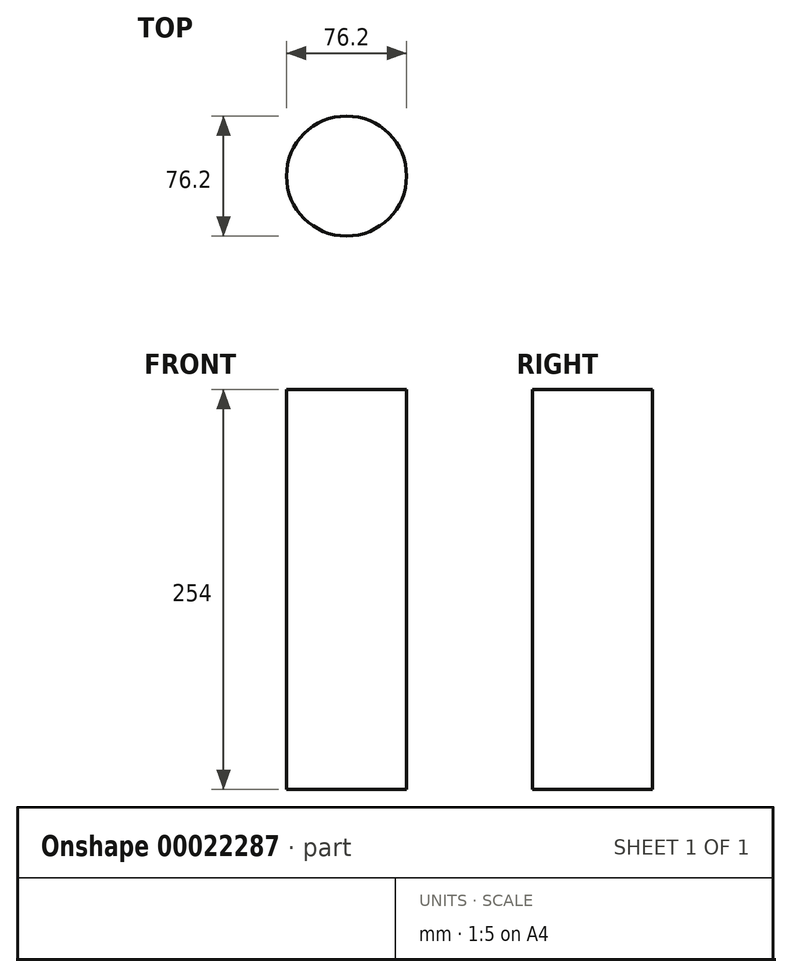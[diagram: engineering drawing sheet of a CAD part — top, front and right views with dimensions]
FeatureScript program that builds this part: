
annotation { "Feature Type Name" : "Feature", "Feature Type Description" : "" }
export const myFeature = defineFeature(function(context is Context, id is Id, definition is map)
    precondition{}
    {
        {
            var Q0;
            Q0=qCreatedBy(makeId("Top.planeOp"),FACE);
            var sketch = newSketch(context, id + "F0", { "sketchPlane" : qUnion([Q0])});
            skCircle(sketch, "E0", {"center": v(0, 0) * mm, "radius": 38.1 * mm});
            skCircle(sketch, "E1", {"center": v(0, 0) * mm, "radius": 12.7 * mm});
            skCircle(sketch, "E2", {"center": v(0, 0) * mm, "radius": 36.83 * mm});
            skLineSegment(sketch, "E3.bottom", {"start": v(12.7, 0) * mm, "end": v(36.76, 0) * mm});
            skLineSegment(sketch, "E3.top", {"start": v(12.7, 2.23) * mm, "end": v(36.76, 2.23) * mm});
            skLineSegment(sketch, "E3.left", {"start": v(12.7, 0) * mm, "end": v(12.7, 2.23) * mm});
            skLineSegment(sketch, "E3.right", {"start": v(36.76, 0) * mm, "end": v(36.76, 2.23) * mm});
            skLineSegment(sketch, "E4.bottom", {"start": v(36.76, 0) * mm, "end": v(12.7, 0) * mm});
            skLineSegment(sketch, "E4.top", {"start": v(36.76, -2.22) * mm, "end": v(12.7, -2.22) * mm});
            skLineSegment(sketch, "E4.left", {"start": v(36.76, 0) * mm, "end": v(36.76, -2.22) * mm});
            skLineSegment(sketch, "E4.right", {"start": v(12.7, 0) * mm, "end": v(12.7, -2.22) * mm});
            skLineSegment(sketch, "E5.bottom", {"start": v(-12.7, 0) * mm, "end": v(-36.76, 0) * mm});
            skLineSegment(sketch, "E5.top", {"start": v(-12.7, -2.22) * mm, "end": v(-36.76, -2.22) * mm});
            skLineSegment(sketch, "E5.left", {"start": v(-12.7, 0) * mm, "end": v(-12.7, -2.22) * mm});
            skLineSegment(sketch, "E5.right", {"start": v(-36.76, 0) * mm, "end": v(-36.76, -2.22) * mm});
            skLineSegment(sketch, "E6.top", {"start": v(-12.7, 2.22) * mm, "end": v(-36.76, 2.22) * mm});
            skLineSegment(sketch, "E6.left", {"start": v(-12.7, 0) * mm, "end": v(-12.7, 2.22) * mm});
            skLineSegment(sketch, "E6.right", {"start": v(-36.76, 0) * mm, "end": v(-36.76, 2.22) * mm});
            skSolve(sketch);
        }
        {
            var Q0;
            Q0=sQuery(id+"F0.wireOp",EDGE,"E0");
            extrude(context, id + "F1", {"bodyType" : ToolBodyType.SURFACE, "surfaceEntities" : qUnion([Q0]), "depth" : 254 * mm});
        }
    });
